# Revit family: TLE26003D_TAC
name_source: partatom
category: 衛生器具
revit_build: Autodesk Revit 2018 (Build: 20170223_1515(x64)
units: mm (PartAtom-declared; Revit-internal decimal feet)

## family parameters
OmniClass タイトル = Sanitary, Laundry, and Cleaning Equipment
OmniClass 番号 = 23.45.00.00
パーツ タイプ = 標準
ロード時にボイドで切り取り = いいえ
丸型コネクタ寸法 = 直径を使用
作業面ベース = いいえ
共有 = いいえ
常に垂直 = はい
部屋計算ポイント = いいえ

## types (1)
- TLE26003D_TAC
    Drain Included = いいえ
    Finish = Polished Chrome
    Height = 316
    Length = 164  [stored 0.538058 ft]
    Material = Brass
    URL = https://www.toto.com
    Voltage = 220~240V
    Water Pressure = Min 0.05MPa Flowing Max 1.0MPa static
    Width = 48
    モデル = TLE26003D/TLE26003H/TLE26008L
    排気配管 = いいえ
    排水配管 = はい
    水配管 = はい
    温水配管 = いいえ
    製造元 = TOTO LTD.
    説明 = TOUCHLESS FAUCET

note: [stored X ft] marks values corroborated as IEEE doubles in the binary element streams (Revit-internal decimal feet)

## geometry (parser evidence)
native form markers: Sweep x2
no freeform markers — native parametric forms only
